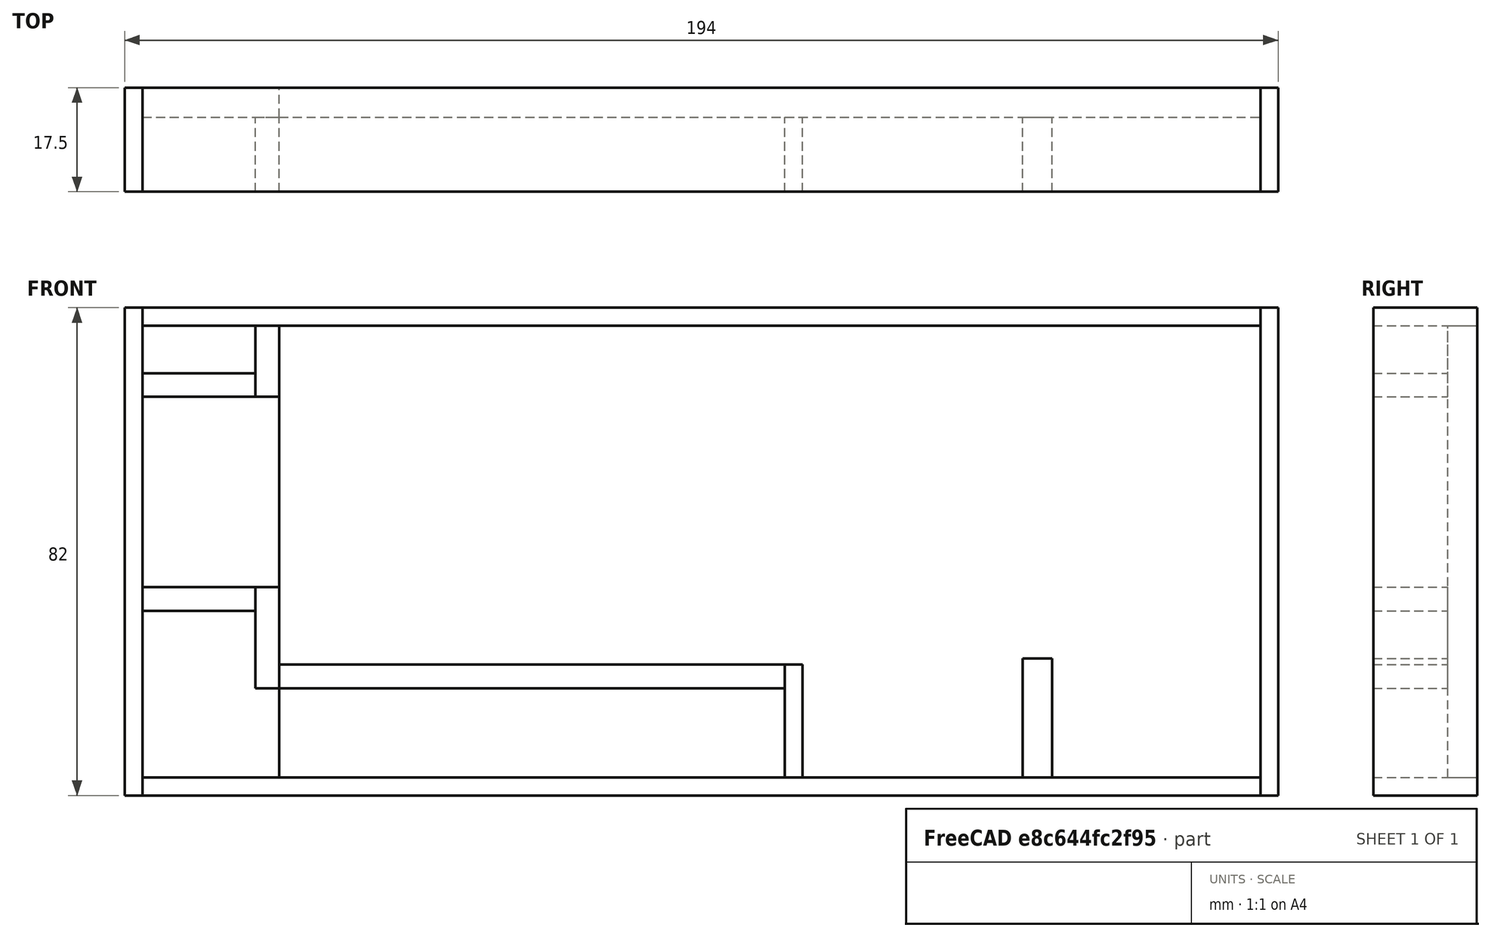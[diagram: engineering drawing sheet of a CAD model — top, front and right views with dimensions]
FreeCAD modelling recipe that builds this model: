
FCSTD DOCUMENT  (FreeCAD 0.15R4671 (Git))
Label: lcd breadboard case 2
License: All rights reserved
LicenseURL: http://en.wikipedia.org/wiki/All_rights_reserved
objects: Part::Box×13
note: 13 computed .brp shape members not serialized (recipe doc carries the construction recipe); baked Part::Feature solids carry a one-line shape summary decoded from their .brp

FEATURE [Part::Box] Box  label="base"
  Height = 76
  Length = 165
  Width = 5
FEATURE [Part::Box] Box001  label="side 001"
  Height = 3
  Length = 188
  Placement = pos=(-23,-12.5,-3) rot=(0,0,1;0rad)
  Width = 17.5
FEATURE [Part::Box] Box002  label="base 002"
  Height = 76
  Length = 23
  Placement = pos=(-23,0,0) rot=(0,0,1;0rad)
  Width = 5
FEATURE [Part::Box] Box003  label="side 002"
  Height = 3
  Length = 188
  Placement = pos=(-23,-12.5,76) rot=(0,0,1;0rad)
  Width = 17.5
FEATURE [Part::Box] Box004  label="side 003"
  Height = 82
  Length = 3
  Placement = pos=(-26,-12.5,-3) rot=(0,0,1;0rad)
  Width = 17.5
FEATURE [Part::Box] Box005  label="side 004"
  Height = 82
  Length = 3
  Placement = pos=(165,-12.5,-3) rot=(0,0,1;0rad)
  Width = 17.5
FEATURE [Part::Box] Box006  label="lcd support 001"
  Height = 20
  Length = 5
  Placement = pos=(125,-12.5,0) rot=(0,0,1;0rad)
  Width = 12.5
FEATURE [Part::Box] Box007  label="lcd support 002"
  Height = 19
  Length = 3
  Placement = pos=(85,-12.5,0) rot=(0,0,1;0rad)
  Width = 12.5
FEATURE [Part::Box] Box008  label="wall 001"
  Height = 4
  Length = 85
  Placement = pos=(0,-12.5,15) rot=(0,0,1;0rad)
  Width = 12.5
FEATURE [Part::Box] Box009  label="wall 002"
  Height = 17
  Length = 4
  Placement = pos=(-4,-12.5,15) rot=(0,0,1;0rad)
  Width = 12.5
FEATURE [Part::Box] Box010  label="wall 003"
  Height = 4
  Length = 19
  Placement = pos=(-23,-12.5,28) rot=(0,0,1;0rad)
  Width = 12.5
FEATURE [Part::Box] Box011  label="wall 004"
  Height = 4
  Length = 19
  Placement = pos=(-23,-12.5,64) rot=(0,0,1;0rad)
  Width = 12.5
FEATURE [Part::Box] Box013  label="wall 005"
  Height = 12
  Length = 4
  Placement = pos=(-4,-12.5,64) rot=(0,0,1;0rad)
  Width = 12.5
